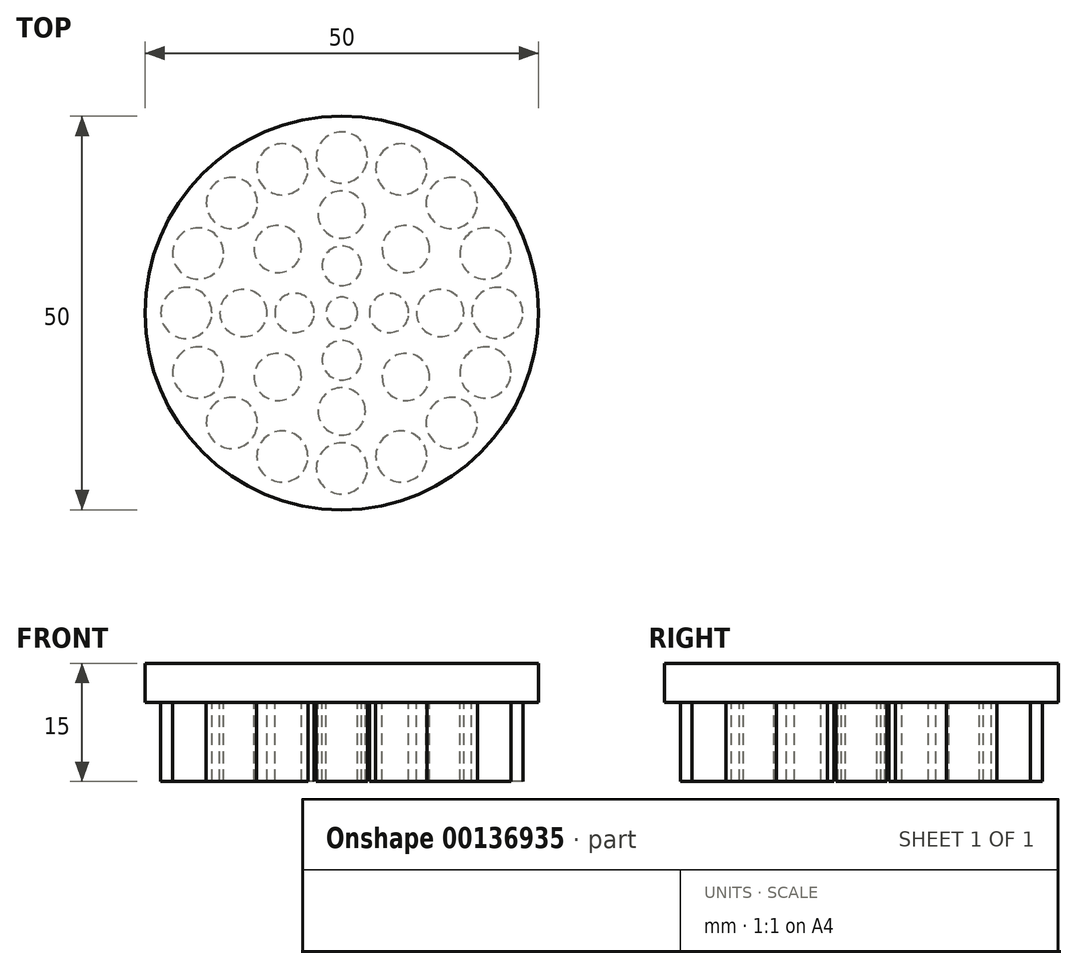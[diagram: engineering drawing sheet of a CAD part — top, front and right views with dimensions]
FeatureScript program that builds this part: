
annotation { "Feature Type Name" : "Feature", "Feature Type Description" : "" }
export const myFeature = defineFeature(function(context is Context, id is Id, definition is map)
    precondition{}
    {
        {
            var Q0;
            Q0=qCreatedBy(makeId("Top.planeOp"),FACE);
            var sketch = newSketch(context, id + "F0", { "sketchPlane" : qUnion([Q0])});
            skCircle(sketch, "E0", {"center": v(0, 0) * mm, "radius": 25 * mm});
            skCircle(sketch, "E1", {"center": v(0, 19.75) * mm, "radius": 3.25 * mm});
            skCircle(sketch, "E2", {"center": v(0, 12.5) * mm, "radius": 3 * mm});
            skCircle(sketch, "E3", {"center": v(0, 6) * mm, "radius": 2.5 * mm});
            skCircle(sketch, "E4", {"center": v(0, 0) * mm, "radius": 2 * mm});
            skCircle(sketch, "E5", {"center": v(6, 0) * mm, "radius": 2.5 * mm});
            skCircle(sketch, "E6", {"center": v(12.5, 0) * mm, "radius": 3 * mm});
            skCircle(sketch, "E7", {"center": v(19.75, 0) * mm, "radius": 3.25 * mm});
            skCircle(sketch, "E8", {"center": v(0, -6) * mm, "radius": 2.5 * mm});
            skCircle(sketch, "E9", {"center": v(0, -12.5) * mm, "radius": 3 * mm});
            skCircle(sketch, "E10", {"center": v(0, -19.75) * mm, "radius": 3.25 * mm});
            skCircle(sketch, "E11", {"center": v(-6, 0) * mm, "radius": 2.5 * mm});
            skCircle(sketch, "E12", {"center": v(-12.5, 0) * mm, "radius": 3 * mm});
            skCircle(sketch, "E13", {"center": v(-19.75, 0) * mm, "radius": 3.25 * mm});
            skCircle(sketch, "E14", {"center": v(13.97, 13.97) * mm, "radius": 3.25 * mm});
            skCircle(sketch, "E15", {"center": v(-13.97, 13.97) * mm, "radius": 3.25 * mm});
            skCircle(sketch, "E16", {"center": v(-13.97, -13.97) * mm, "radius": 3.25 * mm});
            skCircle(sketch, "E17", {"center": v(13.97, -13.97) * mm, "radius": 3.25 * mm});
            skCircle(sketch, "E18", {"center": v(8.13, -8.13) * mm, "radius": 3 * mm});
            skCircle(sketch, "E19", {"center": v(8.13, 8.13) * mm, "radius": 3 * mm});
            skCircle(sketch, "E20", {"center": v(-8.13, 8.13) * mm, "radius": 3 * mm});
            skCircle(sketch, "E21", {"center": v(-8.13, -8.13) * mm, "radius": 3 * mm});
            skCircle(sketch, "E22", {"center": v(-18.25, 7.56) * mm, "radius": 3.25 * mm});
            skCircle(sketch, "E23", {"center": v(-7.56, 18.25) * mm, "radius": 3.25 * mm});
            skCircle(sketch, "E24", {"center": v(7.56, 18.25) * mm, "radius": 3.25 * mm});
            skCircle(sketch, "E25", {"center": v(-18.25, -7.56) * mm, "radius": 3.25 * mm});
            skCircle(sketch, "E26", {"center": v(7.56, -18.25) * mm, "radius": 3.25 * mm});
            skCircle(sketch, "E27", {"center": v(-7.56, -18.25) * mm, "radius": 3.25 * mm});
            skCircle(sketch, "E28", {"center": v(18.25, -7.56) * mm, "radius": 3.25 * mm});
            skCircle(sketch, "E29", {"center": v(18.25, 7.56) * mm, "radius": 3.25 * mm});
            skSolve(sketch);
        }
        {
            var Q0;
            Q0=makeQuery(id+"F0.imprint","IMPRINT",FACE,{"disambiguationData":[TD([[makeQuery(id+"F0.imprint","IMPRINT",EDGE,{"derivedFrom":sQuery(id+"F0.wireOp",EDGE,"E0")}),1.0]])]});
            extrude(context, id + "F1", {"entities" : qUnion([Q0]), "depth" : 5 * mm});
        }
        {
            var Q0;
            Q0=makeQuery(id+"F1.opExtrude","CAP_FACE",FACE,{"disambiguationData":[OSD([sQuery(id+"F0.wireOp",EDGE,"E0"),sQuery(id+"F0.wireOp",EDGE,"E1"),sQuery(id+"F0.wireOp",EDGE,"E2"),sQuery(id+"F0.wireOp",EDGE,"E3"),sQuery(id+"F0.wireOp",EDGE,"E4"),sQuery(id+"F0.wireOp",EDGE,"E5"),sQuery(id+"F0.wireOp",EDGE,"E6"),sQuery(id+"F0.wireOp",EDGE,"E7"),sQuery(id+"F0.wireOp",EDGE,"E8"),sQuery(id+"F0.wireOp",EDGE,"E9"),sQuery(id+"F0.wireOp",EDGE,"E10"),sQuery(id+"F0.wireOp",EDGE,"E11"),sQuery(id+"F0.wireOp",EDGE,"E12"),sQuery(id+"F0.wireOp",EDGE,"E13"),sQuery(id+"F0.wireOp",EDGE,"E14"),sQuery(id+"F0.wireOp",EDGE,"E15"),sQuery(id+"F0.wireOp",EDGE,"E16"),sQuery(id+"F0.wireOp",EDGE,"E17"),sQuery(id+"F0.wireOp",EDGE,"E18"),sQuery(id+"F0.wireOp",EDGE,"E19"),sQuery(id+"F0.wireOp",EDGE,"E20"),sQuery(id+"F0.wireOp",EDGE,"E21"),sQuery(id+"F0.wireOp",EDGE,"E22"),sQuery(id+"F0.wireOp",EDGE,"E23"),sQuery(id+"F0.wireOp",EDGE,"E24"),sQuery(id+"F0.wireOp",EDGE,"E25"),sQuery(id+"F0.wireOp",EDGE,"E26"),sQuery(id+"F0.wireOp",EDGE,"E27"),sQuery(id+"F0.wireOp",EDGE,"E28"),sQuery(id+"F0.wireOp",EDGE,"E29")])],"isStart":false});
            var sketch = newSketch(context, id + "F2", { "sketchPlane" : qUnion([Q0])});
            skCircle(sketch, "E30", {"center": v(0, 0) * mm, "radius": 2 * mm});
            skCircle(sketch, "E31", {"center": v(-6, 0) * mm, "radius": 2.5 * mm});
            skCircle(sketch, "E32", {"center": v(-12.5, 0) * mm, "radius": 3 * mm});
            skCircle(sketch, "E33", {"center": v(-19.75, 0) * mm, "radius": 3.25 * mm});
            skCircle(sketch, "E34", {"center": v(6, 0) * mm, "radius": 2.5 * mm});
            skCircle(sketch, "E35", {"center": v(12.5, 0) * mm, "radius": 3 * mm});
            skCircle(sketch, "E36", {"center": v(19.75, 0) * mm, "radius": 3.25 * mm});
            skCircle(sketch, "E37", {"center": v(0, -6) * mm, "radius": 2.5 * mm});
            skCircle(sketch, "E38", {"center": v(0, -12.5) * mm, "radius": 3 * mm});
            skCircle(sketch, "E39", {"center": v(0, -19.75) * mm, "radius": 3.25 * mm});
            skCircle(sketch, "E40", {"center": v(0, 6) * mm, "radius": 2.5 * mm});
            skCircle(sketch, "E41", {"center": v(0, 12.5) * mm, "radius": 3 * mm});
            skCircle(sketch, "E42", {"center": v(0, 19.75) * mm, "radius": 3.25 * mm});
            skCircle(sketch, "E43", {"center": v(-8.13, 8.13) * mm, "radius": 3 * mm});
            skCircle(sketch, "E44", {"center": v(8.13, 8.13) * mm, "radius": 3 * mm});
            skCircle(sketch, "E45", {"center": v(8.13, -8.13) * mm, "radius": 3 * mm});
            skCircle(sketch, "E46", {"center": v(-8.13, -8.13) * mm, "radius": 3 * mm});
            skCircle(sketch, "E47", {"center": v(-7.56, 18.25) * mm, "radius": 3.25 * mm});
            skCircle(sketch, "E48", {"center": v(-13.97, 13.97) * mm, "radius": 3.25 * mm});
            skCircle(sketch, "E49", {"center": v(-18.25, 7.56) * mm, "radius": 3.25 * mm});
            skCircle(sketch, "E50", {"center": v(7.56, 18.25) * mm, "radius": 3.25 * mm});
            skCircle(sketch, "E51", {"center": v(13.97, 13.97) * mm, "radius": 3.25 * mm});
            skCircle(sketch, "E52", {"center": v(18.25, 7.56) * mm, "radius": 3.25 * mm});
            skCircle(sketch, "E53", {"center": v(18.25, -7.56) * mm, "radius": 3.25 * mm});
            skCircle(sketch, "E54", {"center": v(13.97, -13.97) * mm, "radius": 3.25 * mm});
            skCircle(sketch, "E55", {"center": v(7.56, -18.25) * mm, "radius": 3.25 * mm});
            skCircle(sketch, "E56", {"center": v(-7.56, -18.25) * mm, "radius": 3.25 * mm});
            skCircle(sketch, "E57", {"center": v(-13.97, -13.97) * mm, "radius": 3.25 * mm});
            skCircle(sketch, "E58", {"center": v(-18.25, -7.56) * mm, "radius": 3.25 * mm});
            skSolve(sketch);
        }
        {
            var Q0;
            Q0=makeQuery(id+"F2.imprint","IMPRINT",FACE,{"disambiguationData":[TD([[makeQuery(id+"F2.imprint","IMPRINT",EDGE,{"derivedFrom":sQuery(id+"F2.wireOp",EDGE,"E33")}),1.0]])]});
            var Q1;
            Q1=makeQuery(id+"F2.imprint","IMPRINT",FACE,{"disambiguationData":[TD([[makeQuery(id+"F2.imprint","IMPRINT",EDGE,{"derivedFrom":sQuery(id+"F2.wireOp",EDGE,"E55")}),1.0]])]});
            var Q2;
            Q2=makeQuery(id+"F2.imprint","IMPRINT",FACE,{"disambiguationData":[TD([[makeQuery(id+"F2.imprint","IMPRINT",EDGE,{"derivedFrom":sQuery(id+"F2.wireOp",EDGE,"E41")}),1.0]])]});
            var Q3;
            Q3=makeQuery(id+"F2.imprint","IMPRINT",FACE,{"disambiguationData":[TD([[makeQuery(id+"F2.imprint","IMPRINT",EDGE,{"derivedFrom":sQuery(id+"F2.wireOp",EDGE,"E36")}),1.0]])]});
            var Q4;
            Q4=makeQuery(id+"F2.imprint","IMPRINT",FACE,{"disambiguationData":[TD([[makeQuery(id+"F2.imprint","IMPRINT",EDGE,{"derivedFrom":sQuery(id+"F2.wireOp",EDGE,"E38")}),1.0]])]});
            var Q5;
            Q5=makeQuery(id+"F2.imprint","IMPRINT",FACE,{"disambiguationData":[TD([[makeQuery(id+"F2.imprint","IMPRINT",EDGE,{"derivedFrom":sQuery(id+"F2.wireOp",EDGE,"E46")}),1.0]])]});
            var Q6;
            Q6=makeQuery(id+"F2.imprint","IMPRINT",FACE,{"disambiguationData":[TD([[makeQuery(id+"F2.imprint","IMPRINT",EDGE,{"derivedFrom":sQuery(id+"F2.wireOp",EDGE,"E34")}),1.0]])]});
            var Q7;
            Q7=makeQuery(id+"F2.imprint","IMPRINT",FACE,{"disambiguationData":[TD([[makeQuery(id+"F2.imprint","IMPRINT",EDGE,{"derivedFrom":sQuery(id+"F2.wireOp",EDGE,"E58")}),1.0]])]});
            var Q8;
            Q8=makeQuery(id+"F2.imprint","IMPRINT",FACE,{"disambiguationData":[TD([[makeQuery(id+"F2.imprint","IMPRINT",EDGE,{"derivedFrom":sQuery(id+"F2.wireOp",EDGE,"E45")}),1.0]])]});
            var Q9;
            Q9=makeQuery(id+"F2.imprint","IMPRINT",FACE,{"disambiguationData":[TD([[makeQuery(id+"F2.imprint","IMPRINT",EDGE,{"derivedFrom":sQuery(id+"F2.wireOp",EDGE,"E40")}),1.0]])]});
            var Q10;
            Q10=makeQuery(id+"F2.imprint","IMPRINT",FACE,{"disambiguationData":[TD([[makeQuery(id+"F2.imprint","IMPRINT",EDGE,{"derivedFrom":sQuery(id+"F2.wireOp",EDGE,"E50")}),1.0]])]});
            var Q11;
            Q11=makeQuery(id+"F2.imprint","IMPRINT",FACE,{"disambiguationData":[TD([[makeQuery(id+"F2.imprint","IMPRINT",EDGE,{"derivedFrom":sQuery(id+"F2.wireOp",EDGE,"E31")}),1.0]])]});
            var Q12;
            Q12=makeQuery(id+"F2.imprint","IMPRINT",FACE,{"disambiguationData":[TD([[makeQuery(id+"F2.imprint","IMPRINT",EDGE,{"derivedFrom":sQuery(id+"F2.wireOp",EDGE,"E47")}),1.0]])]});
            var Q13;
            Q13=makeQuery(id+"F2.imprint","IMPRINT",FACE,{"disambiguationData":[TD([[makeQuery(id+"F2.imprint","IMPRINT",EDGE,{"derivedFrom":sQuery(id+"F2.wireOp",EDGE,"E54")}),1.0]])]});
            var Q14;
            Q14=makeQuery(id+"F2.imprint","IMPRINT",FACE,{"disambiguationData":[TD([[makeQuery(id+"F2.imprint","IMPRINT",EDGE,{"derivedFrom":sQuery(id+"F2.wireOp",EDGE,"E52")}),1.0]])]});
            var Q15;
            Q15=makeQuery(id+"F2.imprint","IMPRINT",FACE,{"disambiguationData":[TD([[makeQuery(id+"F2.imprint","IMPRINT",EDGE,{"derivedFrom":sQuery(id+"F2.wireOp",EDGE,"E48")}),1.0]])]});
            var Q16;
            Q16=makeQuery(id+"F2.imprint","IMPRINT",FACE,{"disambiguationData":[TD([[makeQuery(id+"F2.imprint","IMPRINT",EDGE,{"derivedFrom":sQuery(id+"F2.wireOp",EDGE,"E57")}),1.0]])]});
            var Q17;
            Q17=makeQuery(id+"F2.imprint","IMPRINT",FACE,{"disambiguationData":[TD([[makeQuery(id+"F2.imprint","IMPRINT",EDGE,{"derivedFrom":sQuery(id+"F2.wireOp",EDGE,"E35")}),1.0]])]});
            var Q18;
            Q18=makeQuery(id+"F2.imprint","IMPRINT",FACE,{"disambiguationData":[TD([[makeQuery(id+"F2.imprint","IMPRINT",EDGE,{"derivedFrom":sQuery(id+"F2.wireOp",EDGE,"E30")}),1.0]])]});
            var Q19;
            Q19=makeQuery(id+"F2.imprint","IMPRINT",FACE,{"disambiguationData":[TD([[makeQuery(id+"F2.imprint","IMPRINT",EDGE,{"derivedFrom":sQuery(id+"F2.wireOp",EDGE,"E43")}),1.0]])]});
            var Q20;
            Q20=makeQuery(id+"F2.imprint","IMPRINT",FACE,{"disambiguationData":[TD([[makeQuery(id+"F2.imprint","IMPRINT",EDGE,{"derivedFrom":sQuery(id+"F2.wireOp",EDGE,"E32")}),1.0]])]});
            var Q21;
            Q21=makeQuery(id+"F2.imprint","IMPRINT",FACE,{"disambiguationData":[TD([[makeQuery(id+"F2.imprint","IMPRINT",EDGE,{"derivedFrom":sQuery(id+"F2.wireOp",EDGE,"E51")}),1.0]])]});
            var Q22;
            Q22=makeQuery(id+"F2.imprint","IMPRINT",FACE,{"disambiguationData":[TD([[makeQuery(id+"F2.imprint","IMPRINT",EDGE,{"derivedFrom":sQuery(id+"F2.wireOp",EDGE,"E53")}),1.0]])]});
            var Q23;
            Q23=makeQuery(id+"F2.imprint","IMPRINT",FACE,{"disambiguationData":[TD([[makeQuery(id+"F2.imprint","IMPRINT",EDGE,{"derivedFrom":sQuery(id+"F2.wireOp",EDGE,"E49")}),1.0]])]});
            var Q24;
            Q24=makeQuery(id+"F2.imprint","IMPRINT",FACE,{"disambiguationData":[TD([[makeQuery(id+"F2.imprint","IMPRINT",EDGE,{"derivedFrom":sQuery(id+"F2.wireOp",EDGE,"E56")}),1.0]])]});
            var Q25;
            Q25=makeQuery(id+"F2.imprint","IMPRINT",FACE,{"disambiguationData":[TD([[makeQuery(id+"F2.imprint","IMPRINT",EDGE,{"derivedFrom":sQuery(id+"F2.wireOp",EDGE,"E44")}),1.0]])]});
            var Q26;
            Q26=makeQuery(id+"F2.imprint","IMPRINT",FACE,{"disambiguationData":[TD([[makeQuery(id+"F2.imprint","IMPRINT",EDGE,{"derivedFrom":sQuery(id+"F2.wireOp",EDGE,"E42")}),1.0]])]});
            var Q27;
            Q27=makeQuery(id+"F2.imprint","IMPRINT",FACE,{"disambiguationData":[TD([[makeQuery(id+"F2.imprint","IMPRINT",EDGE,{"derivedFrom":sQuery(id+"F2.wireOp",EDGE,"E39")}),1.0]])]});
            var Q28;
            Q28=makeQuery(id+"F2.imprint","IMPRINT",FACE,{"disambiguationData":[TD([[makeQuery(id+"F2.imprint","IMPRINT",EDGE,{"derivedFrom":sQuery(id+"F2.wireOp",EDGE,"E37")}),1.0]])]});
            extrude(context, id + "F3", {"entities" : qUnion([Q0, Q1, Q2, Q3, Q4, Q5, Q6, Q7, Q8, Q9, Q10, Q11, Q12, Q13, Q14, Q15, Q16, Q17, Q18, Q19, Q20, Q21, Q22, Q23, Q24, Q25, Q26, Q27, Q28]), "operationType" : NewBodyOperationType.ADD, "oppositeDirection" : true, "depth" : 15 * mm});
        }
    });
